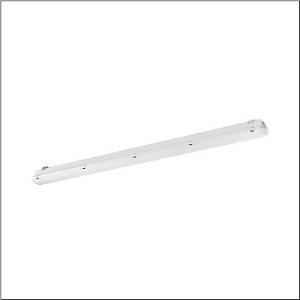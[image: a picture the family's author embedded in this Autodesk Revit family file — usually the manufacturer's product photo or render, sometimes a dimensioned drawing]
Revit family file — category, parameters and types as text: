
# Revit family: monsun_r__11xtreme_mo_51fe107p460j005_a9bb
name_source: partatom
category: Lighting Fixtures
units: mm (PartAtom-declared; Revit-internal decimal feet)

## family parameters
Cut with Voids When Loaded = No
Host = Face
Light Source = No
Part Type = Normal
Room Calculation Point = No
Round Connector Dimension = Use Diameter
Shared = No

## types (1)
- Monsun® 11Xtreme MO (1 x LED, 6370 lm, 34.9 W, 4000K)
    Apparent Load = 35 VA
    CIE Flux Codes = 47 77 93 94 100
    Color Rendering = 80
    Color Temperature = 4000K
    Default Elevation = 1800 mm
    Description = Monsun® 11Xtreme MO, damp-proof luminaire, chain hanger, primary optical cover: enclosure, of PMMA, light emission: direct distribution, primary light characteristic: symmetric, installation type: suspended mounting, surface-mounted, horizontal mounting, vertical mounting, LED, rated luminous flux: 6.370lm, luminous efficacy: 175lm/W, light colour: 840, colour temperature: 4000K, control gear: ON/OFF, with terminal, 3-pole, max. 2.5mm², through-wiring: 5x 2.5mm², mains connection: 220..240V, AC, 50/60Hz, rated input power: 37W, luminaire housing, of glass-fibre reinforced polyester, uncoated, bright grey, incl. chain hanger, length: 1.590mm, width: 90mm, height: 88mm, clip for enclosure, of stainless steel (V2A), ceiling mounting element, of stainless steel (V2A), chain hanger, of stainless steel (V2A), protection rating (complete): IP66, insulation class (complete): insulation class I (protective earthing), certification: CE, ENEC, VDE, UKCA, protection symbol: D, impact resistance: IK04, permissible operating ambient temperature: -35..+50°C, standard: EN 60598-2-1, EN 50419, corresponds to IFS (International Featured Standards) requirements for safety and quality in the food industry, for indoor or canopied outdoor use, no direct snow, no direct sun, no direct rain, contact your sales advisor before using the luminaires in applications with unclear chemical exposure, large temperature fluctuations or condensation-forming humidity, LABS conformity tested according to VDMA 24364:2018-05, packaging unit: 1 piece
    Height = 88 mm
    Lamp = 1 x LED
    Lamp Light Flux = 6370 lm
    Lamp Power = 34.9 W
    Lamp count = 1
    Length = 1590 mm
    Luminous efficacy = 183 lm/W
    Manufacturer = Siteco
    ModVariant = No
    Model = 51FE107P460J005
    Mounting Place = Ceiling
    Mounting Type = Surface mounted
    Number of Poles = 1
    OnlyDefault = Yes
    Power Factor = 1
    Product Name = Monsun® 11Xtreme MO
    Product group = damp-proof luminaire
    ProductGroupID = 300
    Protection Class = Protection class I
    Protection Degree = IP 66
    RLX_Detail_Level = 1
    RLX_Emergency_Light_Flux = 0 lm
    RLX_Emergency_Type = 0
    RLX_Emergency_Type_DB = No
    RlxData = <blob elided: 12429 chars, md5=8fac8575>
    Socket = socket
    Standby Power = 0 W
    System Light Flux = 6370 lm
    System Power = 35 W
    Type Comments = Product without accessories
    Type Image = l_1349234.jpg
    URL = http://relux.com
    VarID = ---
    Voltage = 0 V
    Weight = 0.00 kg
    Width = 90 mm

## geometry (parser evidence)
native form markers: Sweep x11
no freeform markers — native parametric forms only
